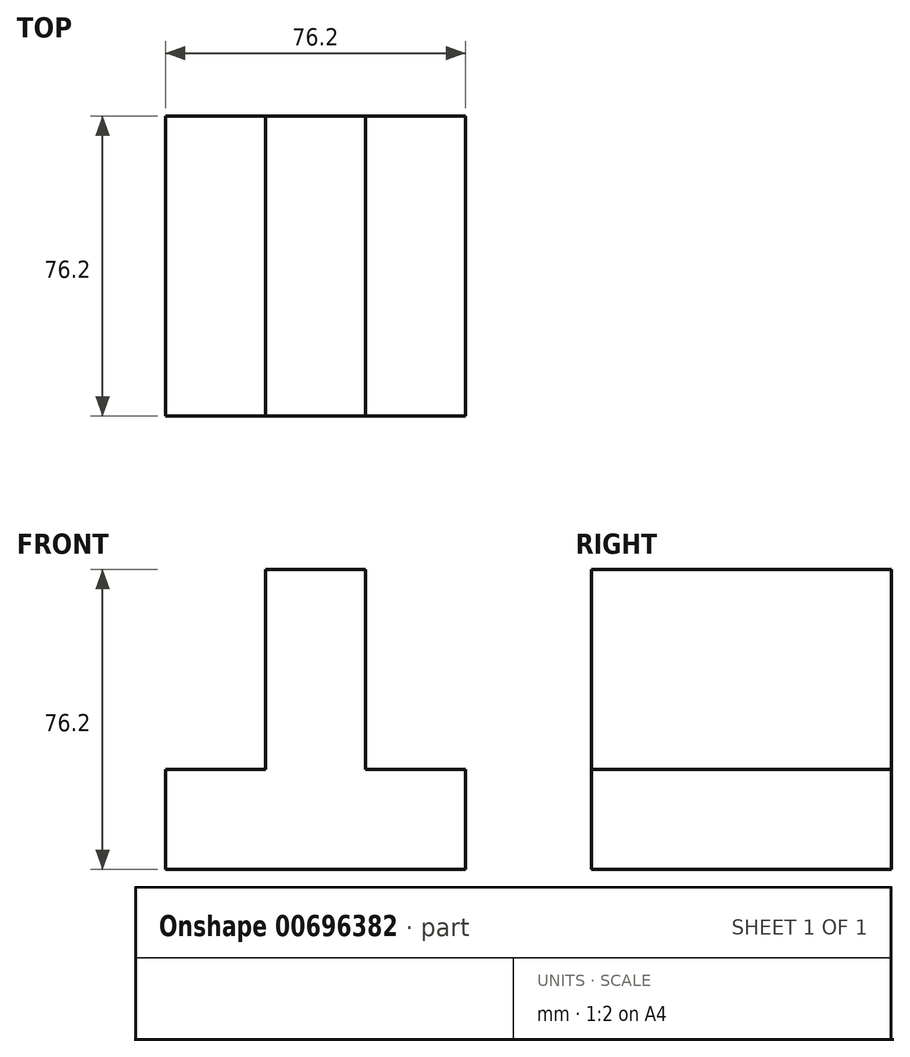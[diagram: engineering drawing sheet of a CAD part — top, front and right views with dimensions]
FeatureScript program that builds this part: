
annotation { "Feature Type Name" : "Feature", "Feature Type Description" : "" }
export const myFeature = defineFeature(function(context is Context, id is Id, definition is map)
    precondition{}
    {
        {
            var Q0;
            Q0=qCreatedBy(makeId("Front.planeOp"),FACE);
            var sketch = newSketch(context, id + "F0", { "sketchPlane" : qUnion([Q0])});
            skLineSegment(sketch, "E0.bottom", {"start": v(0, 0) * mm, "end": v(-76.2, 0) * mm});
            skLineSegment(sketch, "E0.top", {"start": v(-25.4, 76.2) * mm, "end": v(-50.8, 76.2) * mm});
            skLineSegment(sketch, "E0.left", {"start": v(0, 0) * mm, "end": v(0, 25.4) * mm});
            skLineSegment(sketch, "E0.right", {"start": v(-76.2, 0) * mm, "end": v(-76.2, 25.4) * mm});
            skLineSegment(sketch, "E1.top", {"start": v(-76.2, 25.4) * mm, "end": v(-50.8, 25.4) * mm});
            skLineSegment(sketch, "E1.right", {"start": v(-50.8, 76.2) * mm, "end": v(-50.8, 25.4) * mm});
            skLineSegment(sketch, "E2.top", {"start": v(0, 25.4) * mm, "end": v(-25.4, 25.4) * mm});
            skLineSegment(sketch, "E2.right", {"start": v(-25.4, 76.2) * mm, "end": v(-25.4, 25.4) * mm});
            skSolve(sketch);
        }
        {
            var Q0;
            Q0=makeQuery(id+"F0.imprint","IMPRINT",FACE,{"disambiguationData":[TD([[makeQuery(id+"F0.imprint","IMPRINT",EDGE,{"derivedFrom":sQuery(id+"F0.wireOp",EDGE,"E0.bottom")}),-1.0]])]});
            extrude(context, id + "F1", {"entities" : qUnion([Q0]), "depth" : 76.2 * mm, "offsetDistance" : 25.4 * mm});
        }
    });
